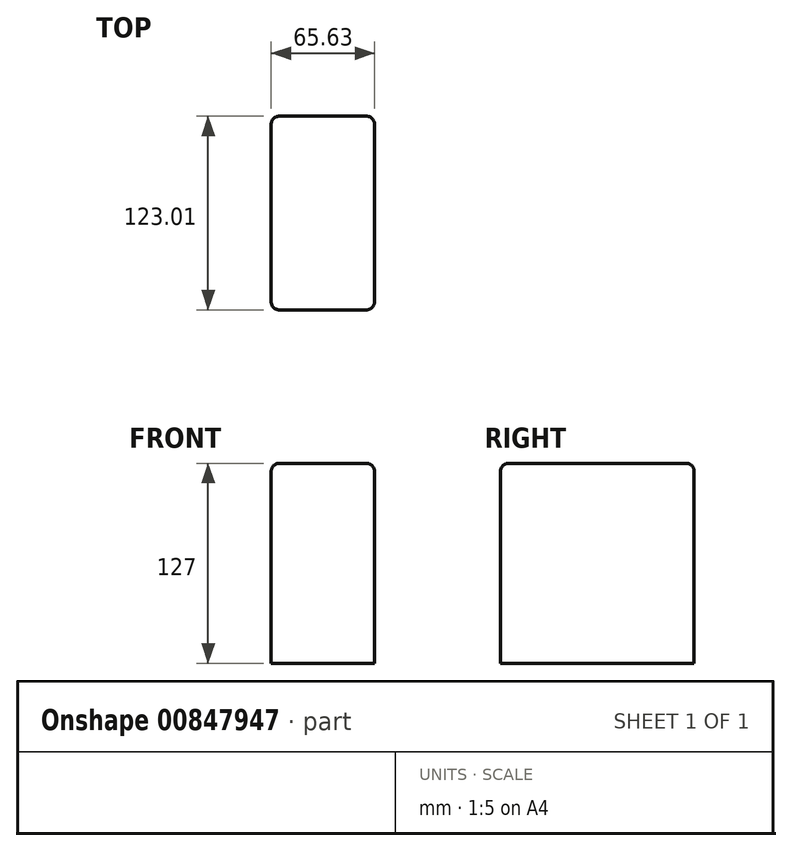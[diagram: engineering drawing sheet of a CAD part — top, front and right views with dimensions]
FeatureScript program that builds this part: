
annotation { "Feature Type Name" : "Feature", "Feature Type Description" : "" }
export const myFeature = defineFeature(function(context is Context, id is Id, definition is map)
    precondition{}
    {
        {
            var Q0;
            Q0=qCreatedBy(makeId("Top.planeOp"),FACE);
            var sketch = newSketch(context, id + "F0", { "sketchPlane" : qUnion([Q0])});
            skLineSegment(sketch, "E0.bottom", {"start": v(-65.63, -55.93) * mm, "end": v(0, -55.93) * mm});
            skLineSegment(sketch, "E0.top", {"start": v(-65.63, 67.08) * mm, "end": v(0, 67.08) * mm});
            skLineSegment(sketch, "E0.left", {"start": v(-65.63, -55.93) * mm, "end": v(-65.63, 67.08) * mm});
            skLineSegment(sketch, "E0.right", {"start": v(0, -55.93) * mm, "end": v(0, 67.08) * mm});
            skSolve(sketch);
        }
        {
            var Q0;
            Q0=makeQuery(id+"F0.imprint","IMPRINT",FACE,{"disambiguationData":[TD([[makeQuery(id+"F0.imprint","IMPRINT",EDGE,{"derivedFrom":sQuery(id+"F0.wireOp",EDGE,"E0.bottom")}),1.0]])]});
            extrude(context, id + "F1", {"entities" : qUnion([Q0]), "depth" : 127 * mm, "offsetDistance" : 25.4 * mm});
        }
        {
            var Q0;
            Q0=makeQuery(id+"F1.opExtrude","CAP_EDGE",EDGE,{"disambiguationData":[OSD([sQuery(id+"F0.wireOp",EDGE,"E0.bottom")])],"isStart":false});
            var Q1;
            Q1=makeQuery(id+"F1.opExtrude","CAP_EDGE",EDGE,{"disambiguationData":[OSD([sQuery(id+"F0.wireOp",EDGE,"E0.left")])],"isStart":false});
            var Q2;
            Q2=makeQuery(id+"F1.opExtrude","CAP_EDGE",EDGE,{"disambiguationData":[OSD([sQuery(id+"F0.wireOp",EDGE,"E0.top")])],"isStart":false});
            var Q3;
            Q3=makeQuery(id+"F1.opExtrude","CAP_EDGE",EDGE,{"disambiguationData":[OSD([sQuery(id+"F0.wireOp",EDGE,"E0.right")])],"isStart":false});
            var Q4;
            Q4=makeQuery(id+"F1.opExtrude","SWEPT_EDGE",EDGE,{"disambiguationData":[OSD([sQuery(id+"F0.wireOp",EDGE,"E0.bottom"),sQuery(id+"F0.wireOp",EDGE,"E0.left")])]});
            var Q5;
            Q5=makeQuery(id+"F1.opExtrude","SWEPT_EDGE",EDGE,{"disambiguationData":[OSD([sQuery(id+"F0.wireOp",EDGE,"E0.bottom"),sQuery(id+"F0.wireOp",EDGE,"E0.right")])]});
            var Q6;
            Q6=makeQuery(id+"F1.opExtrude","SWEPT_EDGE",EDGE,{"disambiguationData":[OSD([sQuery(id+"F0.wireOp",EDGE,"E0.top"),sQuery(id+"F0.wireOp",EDGE,"E0.right")])]});
            var Q7;
            Q7=makeQuery(id+"F1.opExtrude","SWEPT_EDGE",EDGE,{"disambiguationData":[OSD([sQuery(id+"F0.wireOp",EDGE,"E0.top"),sQuery(id+"F0.wireOp",EDGE,"E0.left")])]});
            fillet(context, id + "F2", {"entities" : qUnion([Q0, Q1, Q2, Q3, Q4, Q5, Q6, Q7]), "radius" : 5.08 * mm, "tangentPropagation" : true, "allowEdgeOverflow" : false});
        }
    });
